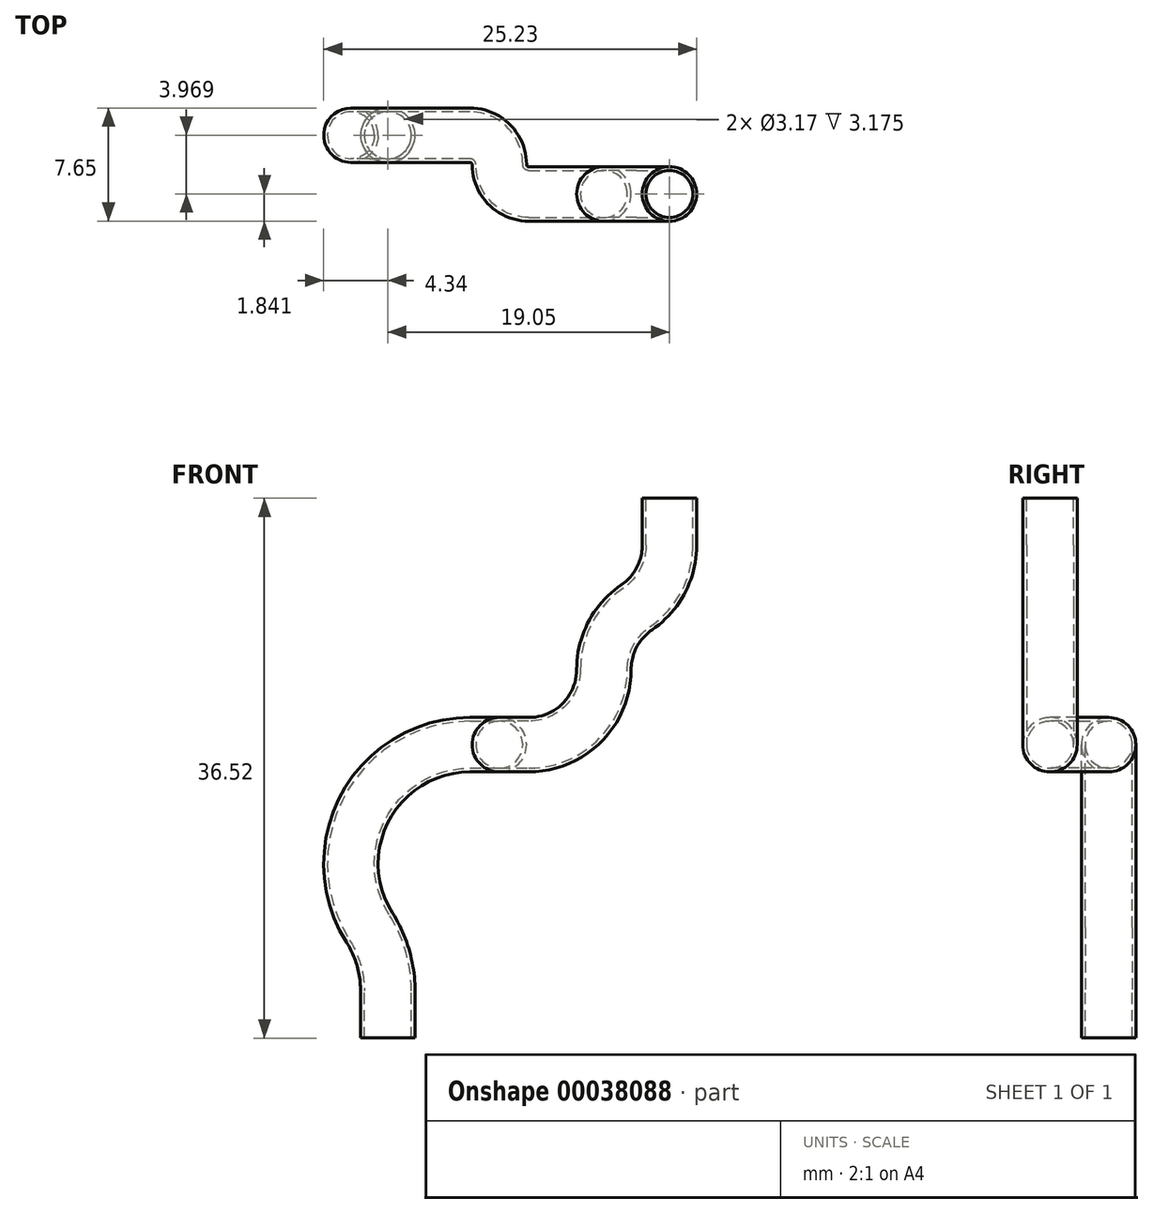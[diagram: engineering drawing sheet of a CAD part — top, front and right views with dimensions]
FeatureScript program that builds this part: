
annotation { "Feature Type Name" : "Feature", "Feature Type Description" : "" }
export const myFeature = defineFeature(function(context is Context, id is Id, definition is map)
    precondition{}
    {
        {
            var Q0;
            Q0=qCreatedBy(makeId("Top.planeOp"),FACE);
            var sketch = newSketch(context, id + "F0", { "sketchPlane" : qUnion([Q0])});
            skCircle(sketch, "E0", {"center": v(0, 0) * mm, "radius": 1.59 * mm});
            skLineSegment(sketch, "E1.rect.bottom", {"start": v(1.84, 1.84) * mm, "end": v(-1.84, 1.84) * mm});
            skLineSegment(sketch, "E1.rect.top", {"start": v(1.84, -1.84) * mm, "end": v(-1.84, -1.84) * mm});
            skLineSegment(sketch, "E1.rect.left", {"start": v(1.84, 1.84) * mm, "end": v(1.84, -1.84) * mm});
            skLineSegment(sketch, "E1.rect.right", {"start": v(-1.84, 1.84) * mm, "end": v(-1.84, -1.84) * mm});
            skSolve(sketch);
        }
        {
            var Q0;
            Q0=qCreatedBy(makeId("Front.planeOp"),FACE);
            var sketch = newSketch(context, id + "F1", { "sketchPlane" : qUnion([Q0])});
            skLineSegment(sketch, "E2", {"start": v(0, 0) * mm, "end": v(0, -5.56) * mm, "construction": true});
            skLineSegment(sketch, "E3", {"start": v(0, 0) * mm, "end": v(5.56, 0) * mm, "construction": true});
            skLineSegment(sketch, "E4", {"start": v(5.56, 0) * mm, "end": v(5.56, 16.67) * mm, "construction": true});
            skLineSegment(sketch, "E5", {"start": v(5.56, 16.67) * mm, "end": v(11.11, 16.67) * mm, "construction": true});
            skArc(sketch, "E6", {"start": v(0, 0) * mm, "mid": v(-0.32, 2.24) * mm, "end": v(-1.25, 4.3) * mm});
            skArc(sketch, "E7", {"start": v(5.56, 16.67) * mm, "mid": v(-1.5, 12.5) * mm, "end": v(-1.25, 4.3) * mm});
            skSolve(sketch);
        }
        {
            var Q0;
            Q0=qCreatedBy(makeId("Top.planeOp"),FACE);
            cPlane(context, id + "F2", {"entities" : qUnion([Q0]), "cplaneType" : CPlaneType.OFFSET, "offset" : 16.67 * mm, "width" : 152.4 * mm, "height" : 152.4 * mm});
        }
        {
            var Q0;
            Q0=qCreatedBy(id+"F2.planeOp",FACE);
            var sketch = newSketch(context, id + "F3", { "sketchPlane" : qUnion([Q0])});
            skLineSegment(sketch, "E8", {"start": v(5.56, 0) * mm, "end": v(0, 0) * mm, "construction": true});
            skLineSegment(sketch, "E9", {"start": v(5.56, 0) * mm, "end": v(5.56, -3.97) * mm, "construction": true});
            skLineSegment(sketch, "E10", {"start": v(5.56, -3.97) * mm, "end": v(9.52, -3.97) * mm, "construction": true});
            skArc(sketch, "E11", {"start": v(7.54, -1.98) * mm, "mid": v(6.96, -0.58) * mm, "end": v(5.56, 0) * mm});
            skArc(sketch, "E12", {"start": v(7.54, -1.98) * mm, "mid": v(8.12, -3.39) * mm, "end": v(9.52, -3.97) * mm});
            skSolve(sketch);
        }
        {
            var Q0;
            Q0=qCreatedBy(makeId("Front.planeOp"),FACE);
            cPlane(context, id + "F4", {"entities" : qUnion([Q0]), "cplaneType" : CPlaneType.OFFSET, "offset" : 3.97 * mm, "width" : 152.4 * mm, "height" : 152.4 * mm});
        }
        {
            var Q0;
            Q0=qCreatedBy(id+"F4.planeOp",FACE);
            var sketch = newSketch(context, id + "F5", { "sketchPlane" : qUnion([Q0])});
            skLineSegment(sketch, "E13", {"start": v(9.52, 16.67) * mm, "end": v(19.05, 16.67) * mm, "construction": true});
            skLineSegment(sketch, "E14", {"start": v(19.05, 16.67) * mm, "end": v(19.05, 30.16) * mm, "construction": true});
            skLineSegment(sketch, "E15", {"start": v(19.05, 30.16) * mm, "end": v(19.05, 33.34) * mm});
            skArc(sketch, "E16", {"start": v(9.52, 16.67) * mm, "mid": v(13.12, 18.16) * mm, "end": v(14.61, 21.76) * mm});
            skArc(sketch, "E17", {"start": v(16.83, 25.96) * mm, "mid": v(18.46, 27.79) * mm, "end": v(19.05, 30.16) * mm});
            skArc(sketch, "E18", {"start": v(16.83, 25.96) * mm, "mid": v(15.2, 24.13) * mm, "end": v(14.61, 21.76) * mm});
            skLineSegment(sketch, "E19", {"start": v(14.61, 21.76) * mm, "end": v(9.52, 21.76) * mm, "construction": true});
            skLineSegment(sketch, "E20", {"start": v(9.53, 16.67) * mm, "end": v(9.53, 21.76) * mm, "construction": true});
            skSolve(sketch);
        }
        {
            var Q0;
            Q0=makeQuery(id+"F0.imprint","IMPRINT",FACE,{"disambiguationData":[TD([[makeQuery(id+"F0.imprint","IMPRINT",EDGE,{"derivedFrom":sQuery(id+"F0.wireOp",EDGE,"E0")}),-1.0]])]});
            var Q1;
            Q1=sQuery(id+"F1.wireOp",EDGE,"E6");
            var Q2;
            Q2=sQuery(id+"F1.wireOp",EDGE,"E7");
            var Q3;
            Q3=sQuery(id+"F3.wireOp",EDGE,"E11");
            var Q4;
            Q4=sQuery(id+"F3.wireOp",EDGE,"E12");
            var Q5;
            Q5=sQuery(id+"F5.wireOp",EDGE,"E16");
            var Q6;
            Q6=sQuery(id+"F5.wireOp",EDGE,"E18");
            var Q7;
            Q7=sQuery(id+"F5.wireOp",EDGE,"E17");
            var Q8;
            Q8=sQuery(id+"F5.wireOp",EDGE,"E15");
            sweep(context, id + "F6", {"profiles" : qUnion([Q0]), "path" : qUnion([Q1, Q2, Q3, Q4, Q5, Q6, Q7, Q8])});
        }
        {
            var Q0;
            Q0=makeQuery(id+"F6.opSweep","SWEPT_EDGE",EDGE,{"disambiguationData":[OSD([sQuery(id+"F0.wireOp",EDGE,"E1.rect.bottom"),sQuery(id+"F0.wireOp",EDGE,"E1.rect.left"),sQuery(id+"F1.wireOp",EDGE,"E6")])]});
            var Q1;
            Q1=makeQuery(id+"F6.opSweep","SWEPT_EDGE",EDGE,{"disambiguationData":[OSD([sQuery(id+"F0.wireOp",EDGE,"E1.rect.bottom"),sQuery(id+"F0.wireOp",EDGE,"E1.rect.right"),sQuery(id+"F1.wireOp",EDGE,"E6")])]});
            var Q2;
            Q2=makeQuery(id+"F6.opSweep","SWEPT_EDGE",EDGE,{"disambiguationData":[OSD([sQuery(id+"F0.wireOp",EDGE,"E1.rect.bottom"),sQuery(id+"F0.wireOp",EDGE,"E1.rect.right"),sQuery(id+"F1.wireOp",EDGE,"E7")])]});
            var Q3;
            Q3=makeQuery(id+"F6.opSweep","SWEPT_EDGE",EDGE,{"disambiguationData":[OSD([sQuery(id+"F0.wireOp",EDGE,"E1.rect.top"),sQuery(id+"F0.wireOp",EDGE,"E1.rect.right"),sQuery(id+"F1.wireOp",EDGE,"E7")])]});
            var Q4;
            Q4=makeQuery(id+"F6.opSweep","SWEPT_EDGE",EDGE,{"disambiguationData":[OSD([sQuery(id+"F0.wireOp",EDGE,"E1.rect.top"),sQuery(id+"F0.wireOp",EDGE,"E1.rect.right"),sQuery(id+"F1.wireOp",EDGE,"E6")])]});
            var Q5;
            Q5=makeQuery(id+"F6.opSweep","SWEPT_EDGE",EDGE,{"disambiguationData":[OSD([sQuery(id+"F0.wireOp",EDGE,"E1.rect.top"),sQuery(id+"F0.wireOp",EDGE,"E1.rect.left"),sQuery(id+"F1.wireOp",EDGE,"E6")])]});
            var Q6;
            Q6=makeQuery(id+"F6.opSweep","SWEPT_EDGE",EDGE,{"disambiguationData":[OSD([sQuery(id+"F0.wireOp",EDGE,"E1.rect.top"),sQuery(id+"F0.wireOp",EDGE,"E1.rect.left"),sQuery(id+"F1.wireOp",EDGE,"E7")])]});
            var Q7;
            Q7=makeQuery(id+"F6.opSweep","SWEPT_EDGE",EDGE,{"disambiguationData":[OSD([sQuery(id+"F0.wireOp",EDGE,"E1.rect.bottom"),sQuery(id+"F0.wireOp",EDGE,"E1.rect.left"),sQuery(id+"F1.wireOp",EDGE,"E7")])]});
            var Q8;
            Q8=makeQuery(id+"F6.opSweep","SWEPT_EDGE",EDGE,{"disambiguationData":[OSD([sQuery(id+"F0.wireOp",EDGE,"E1.rect.bottom"),sQuery(id+"F0.wireOp",EDGE,"E1.rect.right"),sQuery(id+"F3.wireOp",EDGE,"256a9dcb-de02-4cbb-9f0a-806b3a9e86cf")])]});
            var Q9;
            Q9=makeQuery(id+"F6.opSweep","SWEPT_EDGE",EDGE,{"disambiguationData":[OSD([sQuery(id+"F0.wireOp",EDGE,"E1.rect.bottom"),sQuery(id+"F0.wireOp",EDGE,"E1.rect.left"),sQuery(id+"F3.wireOp",EDGE,"256a9dcb-de02-4cbb-9f0a-806b3a9e86cf")])]});
            var Q10;
            Q10=makeQuery(id+"F6.opSweep","SWEPT_EDGE",EDGE,{"disambiguationData":[OSD([sQuery(id+"F0.wireOp",EDGE,"E1.rect.bottom"),sQuery(id+"F0.wireOp",EDGE,"E1.rect.right"),sQuery(id+"F3.wireOp",EDGE,"498e36f3-c2f1-4663-a7d0-804bd8504c1b")])]});
            var Q11;
            Q11=makeQuery(id+"F6.opSweep","SWEPT_EDGE",EDGE,{"disambiguationData":[OSD([sQuery(id+"F0.wireOp",EDGE,"E1.rect.bottom"),sQuery(id+"F0.wireOp",EDGE,"E1.rect.left"),sQuery(id+"F3.wireOp",EDGE,"498e36f3-c2f1-4663-a7d0-804bd8504c1b")])]});
            var Q12;
            Q12=makeQuery(id+"F6.opSweep","SWEPT_EDGE",EDGE,{"disambiguationData":[OSD([sQuery(id+"F0.wireOp",EDGE,"E1.rect.top"),sQuery(id+"F0.wireOp",EDGE,"E1.rect.right"),sQuery(id+"F3.wireOp",EDGE,"256a9dcb-de02-4cbb-9f0a-806b3a9e86cf")])]});
            var Q13;
            Q13=makeQuery(id+"F6.opSweep","SWEPT_EDGE",EDGE,{"disambiguationData":[OSD([sQuery(id+"F0.wireOp",EDGE,"E1.rect.top"),sQuery(id+"F0.wireOp",EDGE,"E1.rect.left"),sQuery(id+"F3.wireOp",EDGE,"256a9dcb-de02-4cbb-9f0a-806b3a9e86cf")])]});
            var Q14;
            Q14=makeQuery(id+"F6.opSweep","SWEPT_EDGE",EDGE,{"disambiguationData":[OSD([sQuery(id+"F0.wireOp",EDGE,"E1.rect.top"),sQuery(id+"F0.wireOp",EDGE,"E1.rect.right"),sQuery(id+"F3.wireOp",EDGE,"498e36f3-c2f1-4663-a7d0-804bd8504c1b")])]});
            var Q15;
            Q15=makeQuery(id+"F6.opSweep","SWEPT_EDGE",EDGE,{"disambiguationData":[OSD([sQuery(id+"F0.wireOp",EDGE,"E1.rect.top"),sQuery(id+"F0.wireOp",EDGE,"E1.rect.left"),sQuery(id+"F3.wireOp",EDGE,"498e36f3-c2f1-4663-a7d0-804bd8504c1b")])]});
            var Q16;
            Q16=makeQuery(id+"F6.opSweep","SWEPT_EDGE",EDGE,{"disambiguationData":[OSD([sQuery(id+"F0.wireOp",EDGE,"E1.rect.top"),sQuery(id+"F0.wireOp",EDGE,"E1.rect.left"),sQuery(id+"F5.wireOp",EDGE,"E16")])]});
            var Q17;
            Q17=makeQuery(id+"F6.opSweep","SWEPT_EDGE",EDGE,{"disambiguationData":[OSD([sQuery(id+"F0.wireOp",EDGE,"E1.rect.top"),sQuery(id+"F0.wireOp",EDGE,"E1.rect.right"),sQuery(id+"F5.wireOp",EDGE,"E16")])]});
            var Q18;
            Q18=makeQuery(id+"F6.opSweep","SWEPT_EDGE",EDGE,{"disambiguationData":[OSD([sQuery(id+"F0.wireOp",EDGE,"E1.rect.bottom"),sQuery(id+"F0.wireOp",EDGE,"E1.rect.right"),sQuery(id+"F5.wireOp",EDGE,"E16")])]});
            var Q19;
            Q19=makeQuery(id+"F6.opSweep","SWEPT_EDGE",EDGE,{"disambiguationData":[OSD([sQuery(id+"F0.wireOp",EDGE,"E1.rect.bottom"),sQuery(id+"F0.wireOp",EDGE,"E1.rect.left"),sQuery(id+"F5.wireOp",EDGE,"E16")])]});
            var Q20;
            Q20=makeQuery(id+"F6.opSweep","SWEPT_EDGE",EDGE,{"disambiguationData":[OSD([sQuery(id+"F0.wireOp",EDGE,"E1.rect.bottom"),sQuery(id+"F0.wireOp",EDGE,"E1.rect.right"),sQuery(id+"F5.wireOp",EDGE,"E18")])]});
            var Q21;
            Q21=makeQuery(id+"F6.opSweep","SWEPT_EDGE",EDGE,{"disambiguationData":[OSD([sQuery(id+"F0.wireOp",EDGE,"E1.rect.bottom"),sQuery(id+"F0.wireOp",EDGE,"E1.rect.left"),sQuery(id+"F5.wireOp",EDGE,"E18")])]});
            var Q22;
            Q22=makeQuery(id+"F6.opSweep","SWEPT_EDGE",EDGE,{"disambiguationData":[OSD([sQuery(id+"F0.wireOp",EDGE,"E1.rect.top"),sQuery(id+"F0.wireOp",EDGE,"E1.rect.right"),sQuery(id+"F5.wireOp",EDGE,"E18")])]});
            var Q23;
            Q23=makeQuery(id+"F6.opSweep","SWEPT_EDGE",EDGE,{"disambiguationData":[OSD([sQuery(id+"F0.wireOp",EDGE,"E1.rect.top"),sQuery(id+"F0.wireOp",EDGE,"E1.rect.right"),sQuery(id+"F5.wireOp",EDGE,"E17")])]});
            var Q24;
            Q24=makeQuery(id+"F6.opSweep","SWEPT_EDGE",EDGE,{"disambiguationData":[OSD([sQuery(id+"F0.wireOp",EDGE,"E1.rect.bottom"),sQuery(id+"F0.wireOp",EDGE,"E1.rect.right"),sQuery(id+"F5.wireOp",EDGE,"E17")])]});
            var Q25;
            Q25=makeQuery(id+"F6.opSweep","SWEPT_EDGE",EDGE,{"disambiguationData":[OSD([sQuery(id+"F0.wireOp",EDGE,"E1.rect.bottom"),sQuery(id+"F0.wireOp",EDGE,"E1.rect.right"),sQuery(id+"F5.wireOp",EDGE,"E15")])]});
            var Q26;
            Q26=makeQuery(id+"F6.opSweep","SWEPT_EDGE",EDGE,{"disambiguationData":[OSD([sQuery(id+"F0.wireOp",EDGE,"E1.rect.top"),sQuery(id+"F0.wireOp",EDGE,"E1.rect.right"),sQuery(id+"F5.wireOp",EDGE,"E15")])]});
            var Q27;
            Q27=makeQuery(id+"F6.opSweep","SWEPT_EDGE",EDGE,{"disambiguationData":[OSD([sQuery(id+"F0.wireOp",EDGE,"E1.rect.bottom"),sQuery(id+"F0.wireOp",EDGE,"E1.rect.left"),sQuery(id+"F5.wireOp",EDGE,"E17")])]});
            var Q28;
            Q28=makeQuery(id+"F6.opSweep","SWEPT_EDGE",EDGE,{"disambiguationData":[OSD([sQuery(id+"F0.wireOp",EDGE,"E1.rect.bottom"),sQuery(id+"F0.wireOp",EDGE,"E1.rect.left"),sQuery(id+"F5.wireOp",EDGE,"E15")])]});
            var Q29;
            Q29=makeQuery(id+"F6.opSweep","SWEPT_EDGE",EDGE,{"disambiguationData":[OSD([sQuery(id+"F0.wireOp",EDGE,"E1.rect.top"),sQuery(id+"F0.wireOp",EDGE,"E1.rect.left"),sQuery(id+"F5.wireOp",EDGE,"E17")])]});
            var Q30;
            Q30=makeQuery(id+"F6.opSweep","SWEPT_EDGE",EDGE,{"disambiguationData":[OSD([sQuery(id+"F0.wireOp",EDGE,"E1.rect.top"),sQuery(id+"F0.wireOp",EDGE,"E1.rect.left"),sQuery(id+"F5.wireOp",EDGE,"E18")])]});
            var Q31;
            Q31=makeQuery(id+"F6.opSweep","SWEPT_EDGE",EDGE,{"disambiguationData":[OSD([sQuery(id+"F0.wireOp",EDGE,"E1.rect.top"),sQuery(id+"F0.wireOp",EDGE,"E1.rect.left"),sQuery(id+"F5.wireOp",EDGE,"E15")])]});
            fillet(context, id + "F7", {"entities" : qUnion([Q0, Q1, Q2, Q3, Q4, Q5, Q6, Q7, Q8, Q9, Q10, Q11, Q12, Q13, Q14, Q15, Q16, Q17, Q18, Q19, Q20, Q21, Q22, Q23, Q24, Q25, Q26, Q27, Q28, Q29, Q30, Q31]), "radius" : 1.84 * mm, "tangentPropagation" : true, "allowEdgeOverflow" : false});
        }
        {
            var Q0;
            Q0=makeQuery(id+"F6.opSweep","CAP_FACE",FACE,{"disambiguationData":[OSD([sQuery(id+"F0.wireOp",EDGE,"E0"),sQuery(id+"F0.wireOp",EDGE,"E1.rect.bottom"),sQuery(id+"F0.wireOp",EDGE,"E1.rect.top"),sQuery(id+"F0.wireOp",EDGE,"E1.rect.left"),sQuery(id+"F0.wireOp",EDGE,"E1.rect.right"),sQuery(id+"F1.wireOp",VERTEX,"E6.start")])],"isStart":true});
            extrude(context, id + "F8", {"entities" : qUnion([Q0]), "operationType" : NewBodyOperationType.ADD, "depth" : 3.17 * mm});
        }
    });
